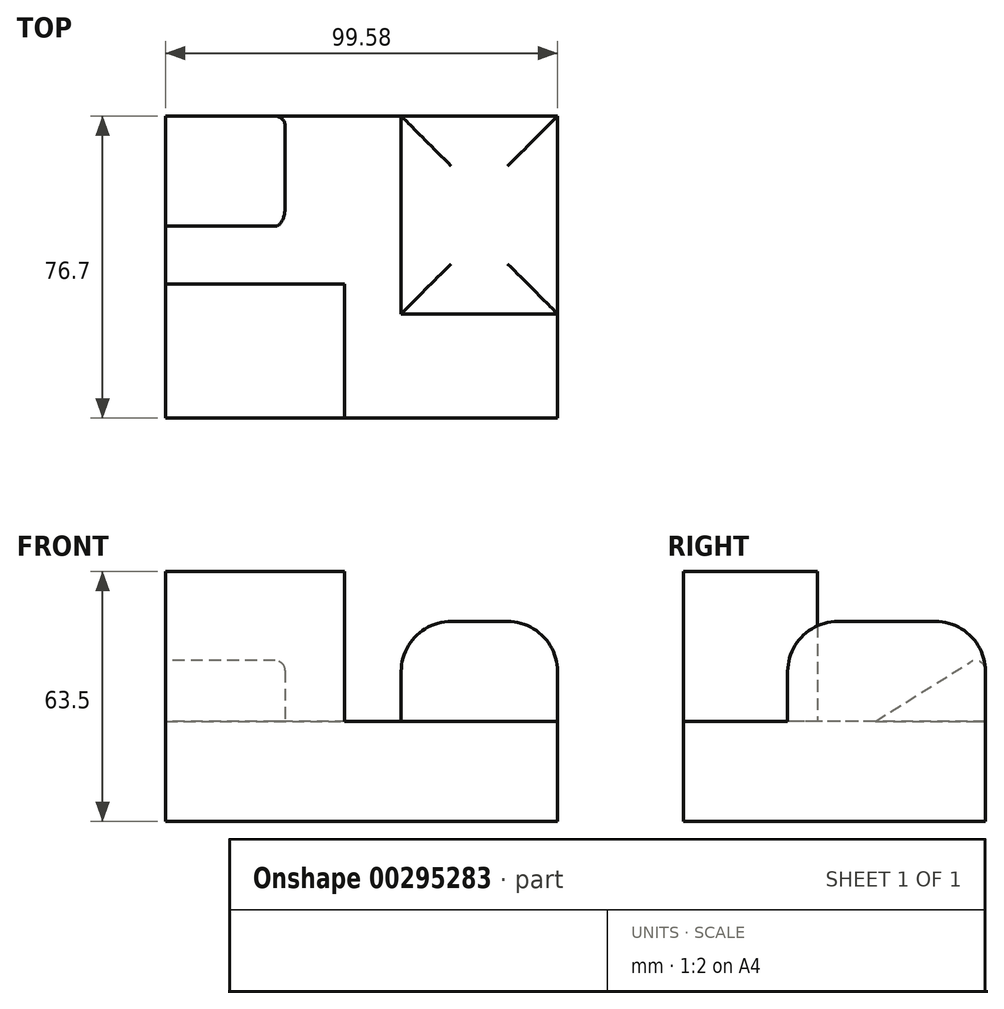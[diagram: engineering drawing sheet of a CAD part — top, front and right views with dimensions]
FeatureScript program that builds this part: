
annotation { "Feature Type Name" : "Feature", "Feature Type Description" : "" }
export const myFeature = defineFeature(function(context is Context, id is Id, definition is map)
    precondition{}
    {
        {
            var Q0;
            Q0=qCreatedBy(makeId("Top.planeOp"),FACE);
            var sketch = newSketch(context, id + "F0", { "sketchPlane" : qUnion([Q0])});
            skLineSegment(sketch, "E0", {"start": v(-43.01, 35.8) * mm, "end": v(-43.01, -40.9) * mm});
            skLineSegment(sketch, "E1", {"start": v(-43.01, -40.9) * mm, "end": v(56.57, -40.9) * mm});
            skLineSegment(sketch, "E2", {"start": v(56.57, -40.9) * mm, "end": v(56.57, 35.8) * mm});
            skLineSegment(sketch, "E3", {"start": v(56.57, 35.8) * mm, "end": v(-43.01, 35.8) * mm});
            skLineSegment(sketch, "E4", {"start": v(-43.01, 7.82) * mm, "end": v(-12.63, 7.82) * mm});
            skLineSegment(sketch, "E5", {"start": v(-12.63, 7.82) * mm, "end": v(-12.63, 35.8) * mm});
            skLineSegment(sketch, "E6", {"start": v(16.84, 35.8) * mm, "end": v(16.84, -14.44) * mm});
            skLineSegment(sketch, "E7", {"start": v(16.84, -14.44) * mm, "end": v(56.57, -14.44) * mm});
            skLineSegment(sketch, "E8", {"start": v(-43.01, -6.92) * mm, "end": v(2.4, -6.92) * mm});
            skLineSegment(sketch, "E9", {"start": v(2.4, -6.92) * mm, "end": v(2.4, -40.9) * mm});
            skSolve(sketch);
        }
        {
            var Q0;
            {var subQ8=sQuery(id+"F0.wireOp",EDGE,"E4");Q0=makeQuery(id+"F0.imprint","IMPRINT",FACE,{"disambiguationData":[TD([[makeQuery(id+"F0.imprint","IMPRINT",EDGE,{"derivedFrom":subQ8}),-1.0]])]});}
            extrude(context, id + "F1", {"entities" : qUnion([Q0]), "depth" : 25.4 * mm});
        }
        {
            var Q0;
            {var subQ3=sQuery(id+"F0.wireOp",EDGE,"E4");Q0=makeQuery(id+"F0.imprint","IMPRINT",FACE,{"disambiguationData":[TD([[makeQuery(id+"F0.imprint","IMPRINT",EDGE,{"derivedFrom":subQ3}),1.0]])]});}
            extrude(context, id + "F2", {"entities" : qUnion([Q0]), "operationType" : NewBodyOperationType.ADD, "depth" : 44.45 * mm});
        }
        {
            var Q0;
            {var subQ4=sQuery(id+"F0.wireOp",EDGE,"E6");Q0=makeQuery(id+"F0.imprint","IMPRINT",FACE,{"disambiguationData":[TD([[makeQuery(id+"F0.imprint","IMPRINT",EDGE,{"derivedFrom":subQ4}),1.0]])]});}
            extrude(context, id + "F3", {"entities" : qUnion([Q0]), "operationType" : NewBodyOperationType.ADD, "depth" : 50.8 * mm});
        }
        {
            var Q0;
            {var subQ3=sQuery(id+"F0.wireOp",EDGE,"E8");Q0=makeQuery(id+"F0.imprint","IMPRINT",FACE,{"disambiguationData":[TD([[makeQuery(id+"F0.imprint","IMPRINT",EDGE,{"derivedFrom":subQ3}),-1.0]])]});}
            extrude(context, id + "F4", {"entities" : qUnion([Q0]), "operationType" : NewBodyOperationType.ADD, "depth" : 63.5 * mm});
        }
        {
            var Q0;
            Q0=makeQuery(id+"F3.opExtrude","CAP_EDGE",EDGE,{"disambiguationData":[OSD([sQuery(id+"F0.wireOp",EDGE,"E7")])],"isStart":false});
            var Q1;
            Q1=makeQuery(id+"F3.opExtrude","CAP_EDGE",EDGE,{"disambiguationData":[OSD([sQuery(id+"F0.wireOp",EDGE,"E2")])],"isStart":false});
            var Q2;
            Q2=makeQuery(id+"F3.opExtrude","CAP_EDGE",EDGE,{"disambiguationData":[OSD([sQuery(id+"F0.wireOp",EDGE,"E3")])],"isStart":false});
            var Q3;
            Q3=makeQuery(id+"F3.opExtrude","CAP_EDGE",EDGE,{"disambiguationData":[OSD([sQuery(id+"F0.wireOp",EDGE,"E6")])],"isStart":false});
            fillet(context, id + "F5", {"entities" : qUnion([Q0, Q1, Q2, Q3]), "radius" : 12.7 * mm, "tangentPropagation" : true, "allowEdgeOverflow" : false});
        }
        {
            var Q0;
            Q0=makeQuery(id+"F2.opExtrude","CAP_EDGE",EDGE,{"disambiguationData":[OSD([sQuery(id+"F0.wireOp",EDGE,"E4")])],"isStart":false});
            chamfer(context, id + "F6", {"entities" : qUnion([Q0]), "chamferType" : ChamferType.OFFSET_ANGLE, "width" : 30.48 * mm, "oppositeDirection" : false, "angle" : 32 * degree, "tangentPropagation" : true});
        }
        {
            var Q0;
            {var subQ0=sQuery(id+"F0.wireOp",EDGE,"E3");Q0=makeQuery(id+"F6.opChamfer","BLEND_EDGE",EDGE,{"blendedFrom":[makeQuery(id+"F2.opExtrude","CAP_EDGE",EDGE,{"disambiguationData":[OSD([sQuery(id+"F0.wireOp",EDGE,"E4")])],"isStart":false}),makeQuery(id+"F3.boolean.opBoolean","MERGE",FACE,{"derivedFrom":[makeQuery(id+"F2.boolean.opBoolean","MERGE",FACE,{"derivedFrom":[makeQuery(id+"F1.opExtrude","SWEPT_FACE",FACE,{"disambiguationData":[OSD([subQ0])]}),makeQuery(id+"F2.opExtrude","SWEPT_FACE",FACE,{"disambiguationData":[OSD([subQ0])]})]}),makeQuery(id+"F3.opExtrude","SWEPT_FACE",FACE,{"disambiguationData":[OSD([subQ0])]})]})],"blendedInto":[makeQuery(id+"F3.boolean.opBoolean","MERGE",FACE,{"derivedFrom":[makeQuery(id+"F2.boolean.opBoolean","MERGE",FACE,{"derivedFrom":[makeQuery(id+"F1.opExtrude","SWEPT_FACE",FACE,{"disambiguationData":[OSD([subQ0])]}),makeQuery(id+"F2.opExtrude","SWEPT_FACE",FACE,{"disambiguationData":[OSD([subQ0])]})]}),makeQuery(id+"F3.opExtrude","SWEPT_FACE",FACE,{"disambiguationData":[OSD([subQ0])]})]})]});}
            fillet(context, id + "F7", {"entities" : qUnion([Q0]), "radius" : 2.54 * mm, "tangentPropagation" : true, "allowEdgeOverflow" : false});
        }
        {
            var Q0;
            Q0=makeQuery(id+"F6.opChamfer","BLEND_EDGE",EDGE,{"blendedFrom":[makeQuery(id+"F2.opExtrude","CAP_EDGE",EDGE,{"disambiguationData":[OSD([sQuery(id+"F0.wireOp",EDGE,"E4")])],"isStart":false}),makeQuery(id+"F2.opExtrude","SWEPT_FACE",FACE,{"disambiguationData":[OSD([sQuery(id+"F0.wireOp",EDGE,"E5")])]})],"blendedInto":[makeQuery(id+"F2.opExtrude","SWEPT_FACE",FACE,{"disambiguationData":[OSD([sQuery(id+"F0.wireOp",EDGE,"E5")])]})]});
            var Q1;
            Q1=makeQuery(id+"F2.opExtrude","SWEPT_EDGE",EDGE,{"disambiguationData":[OSD([sQuery(id+"F0.wireOp",EDGE,"E3"),sQuery(id+"F0.wireOp",EDGE,"E5")])]});
            fillet(context, id + "F8", {"entities" : qUnion([Q0, Q1]), "radius" : 2.54 * mm, "tangentPropagation" : true, "allowEdgeOverflow" : false});
        }
    });
